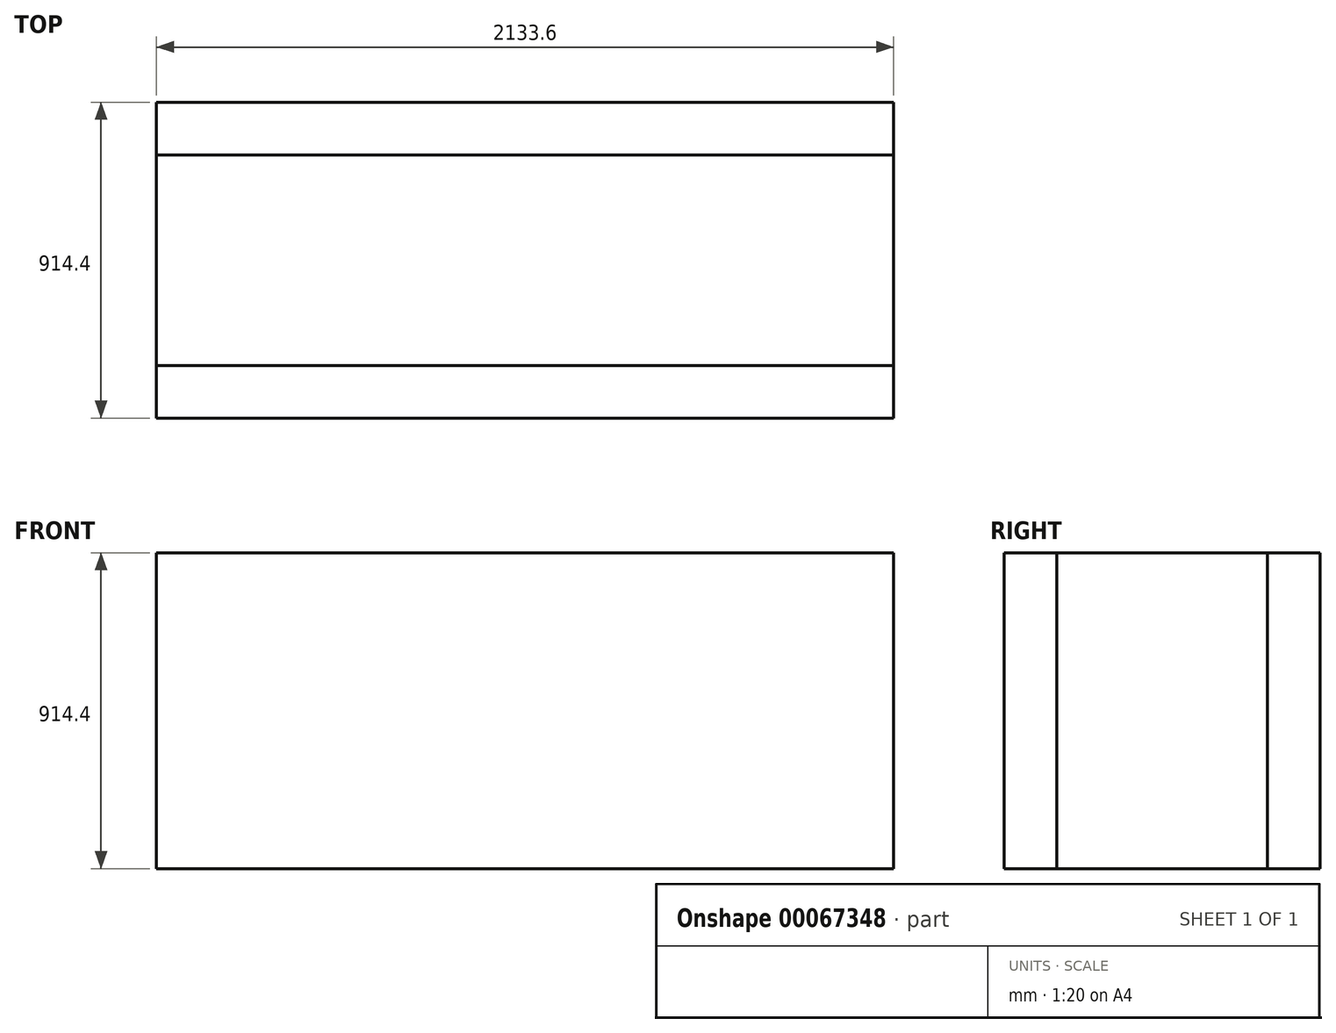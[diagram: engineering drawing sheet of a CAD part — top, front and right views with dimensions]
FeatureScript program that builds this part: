
annotation { "Feature Type Name" : "Feature", "Feature Type Description" : "" }
export const myFeature = defineFeature(function(context is Context, id is Id, definition is map)
    precondition{}
    {
        {
            var Q0;
            Q0=qCreatedBy(makeId("Top.planeOp"),FACE);
            var sketch = newSketch(context, id + "F0", { "sketchPlane" : qUnion([Q0])});
            skLineSegment(sketch, "E0.bottom", {"start": v(1066.8, 304.8) * mm, "end": v(-1066.8, 304.8) * mm});
            skLineSegment(sketch, "E0.top", {"start": v(1066.8, -304.8) * mm, "end": v(-1066.8, -304.8) * mm});
            skLineSegment(sketch, "E0.left", {"start": v(1066.8, 304.8) * mm, "end": v(1066.8, -304.8) * mm});
            skLineSegment(sketch, "E0.right", {"start": v(-1066.8, 304.8) * mm, "end": v(-1066.8, -304.8) * mm});
            skPoint(sketch, "E0.middle", {"position": v(0, 0) * mm});
            skLineSegment(sketch, "E1.bottom", {"start": v(1066.8, 457.2) * mm, "end": v(-1066.8, 457.2) * mm});
            skLineSegment(sketch, "E1.top", {"start": v(1066.8, -457.2) * mm, "end": v(-1066.8, -457.2) * mm});
            skLineSegment(sketch, "E1.left", {"start": v(1066.8, 457.2) * mm, "end": v(1066.8, -457.2) * mm});
            skLineSegment(sketch, "E1.right", {"start": v(-1066.8, 457.2) * mm, "end": v(-1066.8, -457.2) * mm});
            skSolve(sketch);
        }
        {
            var Q0;
            {var subQ0=sQuery(id+"F0.wireOp",EDGE,"E0.bottom");Q0=makeQuery(id+"F0.imprint","IMPRINT",FACE,{"disambiguationData":[TD([[makeQuery(id+"F0.imprint","IMPRINT",EDGE,{"derivedFrom":subQ0}),1.0]])]});}
            extrude(context, id + "F1", {"entities" : qUnion([Q0]), "depth" : 914.4 * mm});
        }
        {
            var Q0;
            {var subQ5=sQuery(id+"F0.wireOp",EDGE,"E1.bottom");Q0=makeQuery(id+"F0.imprint","IMPRINT",FACE,{"disambiguationData":[TD([[makeQuery(id+"F0.imprint","IMPRINT",EDGE,{"derivedFrom":subQ5}),1.0]])]});}
            var Q1;
            {var subQ0=sQuery(id+"F0.wireOp",EDGE,"E1.left");var subQ1=sQuery(id+"F0.wireOp",EDGE,"E0.bottom");var subQ2=makeQuery(id+"F0.imprint","INTERSECT",VERTEX,{"derivedFrom":[subQ1,subQ0]});Q1=makeQuery(id+"F0.imprint","IMPRINT",FACE,{"disambiguationData":[TD([[makeQuery(id+"F0.imprint","IMPRINT",EDGE,{"disambiguationData":[TD([[subQ2,-1.0]])],"derivedFrom":subQ1}),1.0]])]});}
            var Q2;
            {var subQ5=sQuery(id+"F0.wireOp",EDGE,"E1.top");Q2=makeQuery(id+"F0.imprint","IMPRINT",FACE,{"disambiguationData":[TD([[makeQuery(id+"F0.imprint","IMPRINT",EDGE,{"derivedFrom":subQ5}),-1.0]])]});}
            extrude(context, id + "F2", {"entities" : qUnion([Q0, Q1, Q2]), "depth" : 914.4 * mm});
        }
    });
